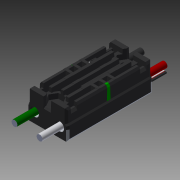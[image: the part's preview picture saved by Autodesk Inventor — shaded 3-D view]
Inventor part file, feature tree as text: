
AUTODESK INVENTOR PART (.ipt)
format: ipt  version: 2016 SP1 (Build 200210100, 210)  size: 4,882,432 bytes
history: native  units: in
note: dims shown in document units (in); Inventor stores cm internally (conversion verified against a paired STEP export)
features: other x2, plane x2, split x2, imported_body x1
ambient origin geometry x8: Origin, YZ Plane, XZ Plane, XY Plane, X Axis, Y Axis, Z Axis, Center Point
bodies: Body1 (feature_tree)
feature tree (7):
  parser-record x1  (decoder bookkeeping rows leaked as tree rows — omitted from the tree; the rows remain in map.json)
  other  "217-9090-STEP-201408141"
  plane  "Work Plane1"
  split  "Split1"
  plane  "Work Plane2"
  split  "Split2"
  imported_body  "Base1"
